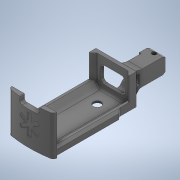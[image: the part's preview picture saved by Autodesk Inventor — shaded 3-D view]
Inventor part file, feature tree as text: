
AUTODESK INVENTOR PART (.ipt)
format: ipt  version: 2020 (Build 240168000, 168)  size: 864,256 bytes
history: native  units: mm
features: projected_geometry x38, extrude x21, sketch x18, fillet x10, other x9, chamfer x2
ambient origin geometry x8: Origin, YZ Plane, XZ Plane, XY Plane, X Axis, Y Axis, Z Axis, Center Point
bodies: Body1 (feature_tree)
feature tree (98):
  other  "Твердое тело1"
  sketch  "Эскиз1"
  extrude  "Выдавливание3"  Depth=202.0mm
  other  "РабПлоскость1"
  extrude  "Выдавливание1"  Depth=35.0mm
  other  "РабПлоскость2"
  sketch  "Эскиз2"
  extrude  "Выдавливание4"  Depth=68.0mm
  extrude  "Выдавливание5"  Depth=2.0mm
  sketch  "Эскиз4"
  extrude  "Выдавливание6"  Depth=2.0mm
  extrude  "Выдавливание7"  Depth=3.0mm
  other  "РабПлоскость3"
  extrude  "Выдавливание8"  Depth=3.0mm
  other  "РабПлоскость4"
  extrude  "Выдавливание9"  Depth=210.0mm
  sketch  "Эскиз8"
  extrude  "Выдавливание10"  Depth=20.0mm TaperAngle=0.0deg
  fillet  "Сопряжение1"  Radius=1.5mm
  fillet  "Сопряжение2"  Radius=28.0mm
  fillet  "Сопряжение3"  Radius=7.0mm
  fillet  "Сопряжение4"  Radius=20.0mm
  fillet  "Сопряжение5"  Radius=13.0mm
  extrude  "Выдавливание11"  Depth=5.0mm
  extrude  "Выдавливание12"  Depth=3.0mm
  fillet  "Сопряжение6"  Radius=10.0mm
  extrude  "Выдавливание13"  Depth=84.0mm
  chamfer  "Фаска1"  Distance=5.0mm
  fillet  "Сопряжение7"  Radius=52.0mm
  sketch  "Эскиз10"
  other  "РабПлоскость5"
  extrude  "Выдавливание14"  Depth=5.0mm TaperAngle=0.0deg
  fillet  "Сопряжение8"  Radius=35.0mm
  extrude  "Выдавливание15"  Depth=18.0mm
  fillet  "Сопряжение9"  Radius=3.0mm
  extrude  "Выдавливание16"  Depth=30.0mm TaperAngle=360.0deg
  fillet  "Сопряжение10"  Radius=0.5mm
  extrude  "Выдавливание17"  TaperAngle=0.0deg  [1 undecoded]
  chamfer  "Фаска2"  Distance=8.0mm
  other  "РабПлоскость10"
  other  "РабПлоскость9"
  sketch  "Эскиз14"
  other  "РабПлоскость8"
  sketch  "Эскиз15"
  sketch  "Эскиз16"
  sketch  "Эскиз17"
  extrude  "Выдавливание20"  Depth=2.0mm
  extrude  "Выдавливание21"  Depth=1.5mm TaperAngle=0.0deg
  extrude  "Выдавливание22"  Depth=2.0mm
  extrude  "Выдавливание23"  Depth=2.5mm
  extrude  "Выдавливание24"  Depth=6.981317mm
  projected_geometry  "Спроецированная петля1"
  projected_geometry  "Спроецированная петля7"
  projected_geometry  "Спроецированная петля8"
  sketch  "Эскиз3"
  projected_geometry  "Спроецированная петля9"
  projected_geometry  "Спроецированная петля10"
  projected_geometry  "Спроецированная петля11"
  projected_geometry  "Спроецированная петля12"
  sketch  "Эскиз5"
  projected_geometry  "Спроецированная петля13"
  projected_geometry  "Спроецированная петля14"
  projected_geometry  "Спроецированная петля15"
  projected_geometry  "Спроецированная петля16"
  projected_geometry  "Спроецированная петля17"
  sketch  "Эскиз6"
  projected_geometry  "Спроецированная петля18"
  projected_geometry  "Спроецированная петля19"
  projected_geometry  "Спроецированная петля20"
  projected_geometry  "Спроецированная петля21"
  projected_geometry  "Спроецированная петля22"
  projected_geometry  "Спроецированная петля23"
  projected_geometry  "Спроецированная петля24"
  projected_geometry  "Спроецированная петля25"
  projected_geometry  "Спроецированная петля26"
  projected_geometry  "Спроецированная петля27"
  projected_geometry  "Спроецированная петля28"
  sketch  "Эскиз9"
  projected_geometry  "Спроецированная петля29"
  projected_geometry  "Спроецированная петля30"
  sketch  "Эскиз11"
  projected_geometry  "Спроецированная петля31"
  projected_geometry  "Спроецированная петля32"
  projected_geometry  "Спроецированная петля33"
  sketch  "Эскиз12"
  projected_geometry  "Спроецированная петля34"
  projected_geometry  "Спроецированная петля35"
  projected_geometry  "Спроецированная петля37"
  sketch  "Эскиз18"
  projected_geometry  "Спроецированная петля38"
  sketch  "Эскиз19"
  projected_geometry  "Спроецированная петля39"
  projected_geometry  "Спроецированная петля40"
  projected_geometry  "Спроецированная петля41"
  sketch  "Эскиз20"
  projected_geometry  "Спроецированная петля42"
  projected_geometry  "Спроецированная петля43"
  projected_geometry  "Спроецированная петля44"
note: 1 required parameter value undecoded (feature->parameter linkage not recoverable at this tier; creation-order binding heuristic only, values carry confidence <= 0.55)
